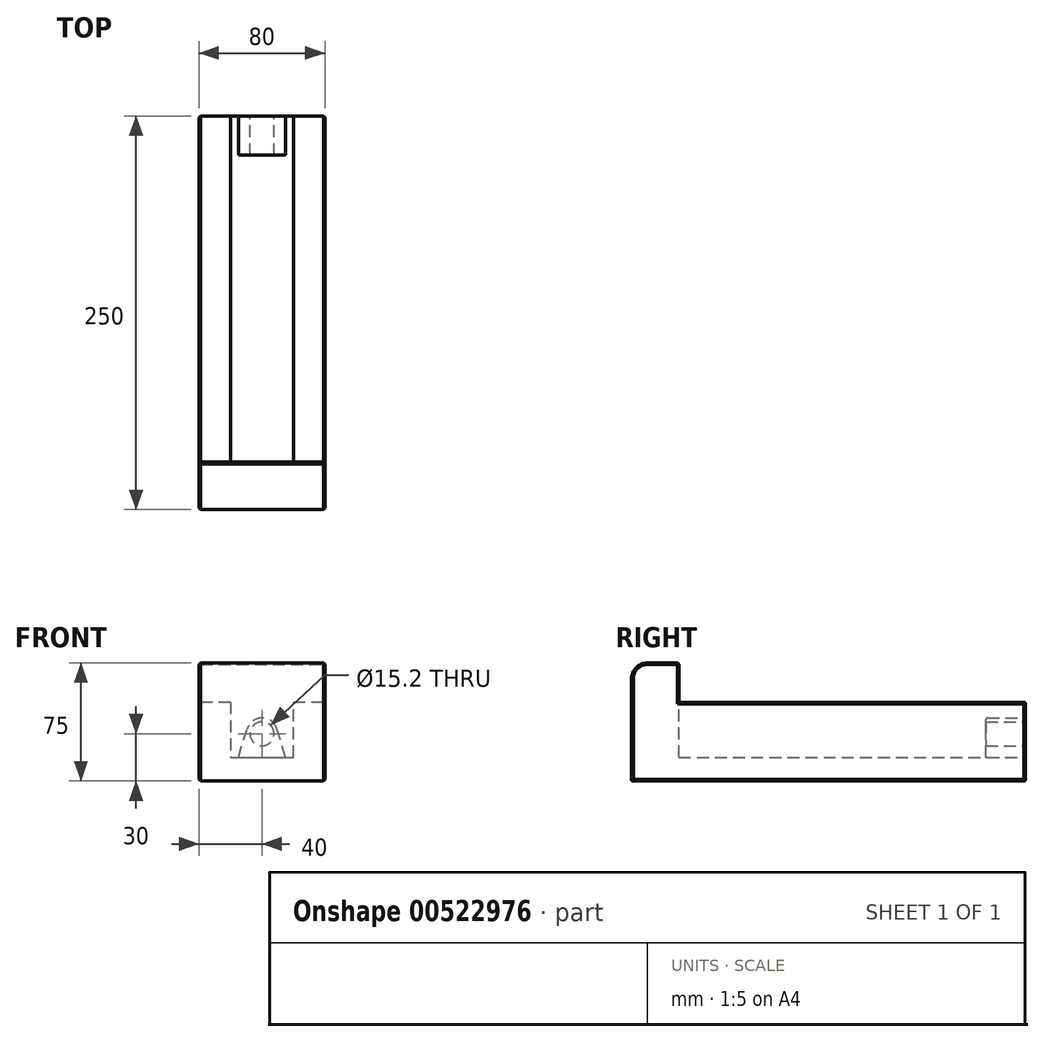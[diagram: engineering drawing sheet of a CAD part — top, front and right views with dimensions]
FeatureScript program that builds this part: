
annotation { "Feature Type Name" : "Feature", "Feature Type Description" : "" }
export const myFeature = defineFeature(function(context is Context, id is Id, definition is map)
    precondition{}
    {
        {
            var Q0;
            Q0=qCreatedBy(makeId("Right.planeOp"),FACE);
            var sketch = newSketch(context, id + "F0", { "sketchPlane" : qUnion([Q0])});
            skLineSegment(sketch, "E0", {"start": v(0, 0) * mm, "end": v(103.84, 0) * mm});
            skLineSegment(sketch, "E1", {"start": v(103.84, 0) * mm, "end": v(103.84, 50) * mm});
            skLineSegment(sketch, "E2", {"start": v(103.84, 50) * mm, "end": v(-116.16, 50) * mm});
            skLineSegment(sketch, "E3", {"start": v(-116.16, 50) * mm, "end": v(-116.16, 75) * mm});
            skLineSegment(sketch, "E4", {"start": v(-116.16, 75) * mm, "end": v(-136.16, 75) * mm});
            skLineSegment(sketch, "E5", {"start": v(-146.16, 65) * mm, "end": v(-146.16, 0) * mm});
            skLineSegment(sketch, "E6", {"start": v(-146.16, 0) * mm, "end": v(45.93, 0) * mm});
            skLineSegment(sketch, "E7", {"start": v(-146.16, 0) * mm, "end": v(103.84, 0) * mm});
            skPoint(sketch, "E8.visualSharp", {"position": v(-146.16, 75) * mm});
            skArc(sketch, "E8.filletArc", {"start": v(-136.16, 75) * mm, "mid": v(-143.23, 72.07) * mm, "end": v(-146.16, 65) * mm});
            skSolve(sketch);
        }
        {
            var Q0;
            Q0 = qSketchRegion(id + "F0", true);
            extrude(context, id + "F1", {"entities" : qUnion([Q0]), "endBound" : BoundingType.SYMMETRIC, "depth" : 80 * mm, "offsetDistance" : 25 * mm});
        }
        {
            var Q0;
            Q0=makeQuery(id+"F1.opExtrude","SWEPT_FACE",FACE,{"disambiguationData":[OSD([sQuery(id+"F0.wireOp",EDGE,"E1")])]});
            var sketch = newSketch(context, id + "F2", { "sketchPlane" : qUnion([Q0])});
            skLineSegment(sketch, "E9", {"start": v(20, 50) * mm, "end": v(20, 15) * mm});
            skLineSegment(sketch, "E10", {"start": v(20, 15) * mm, "end": v(-20, 15) * mm});
            skLineSegment(sketch, "E11", {"start": v(-20, 15) * mm, "end": v(-20, 50) * mm});
            skCircle(sketch, "E12", {"center": v(0, 30) * mm, "radius": 10 * mm});
            skPoint(sketch, "E12.centerSnap0", {"position": v(0, 15) * mm});
            skLineSegment(sketch, "E13", {"start": v(-15, 15) * mm, "end": v(-9.57, 32.9) * mm});
            skLineSegment(sketch, "E14", {"start": v(15, 15) * mm, "end": v(9.57, 32.9) * mm});
            skLineSegment(sketch, "E15", {"start": v(-20, 50) * mm, "end": v(20, 50) * mm});
            skCircle(sketch, "E16", {"center": v(0, 30) * mm, "radius": 7.6 * mm});
            skSolve(sketch);
        }
        {
            var Q0;
            {var subQ2=sQuery(id+"F2.wireOp",EDGE,"E9");Q0=makeQuery(id+"F2.imprint","IMPRINT",FACE,{"disambiguationData":[TD([[makeQuery(id+"F2.imprint","IMPRINT",EDGE,{"derivedFrom":subQ2}),-1.0]])]});}
            var Q1;
            {var subQ4=sQuery(id+"F2.wireOp",EDGE,"E11");Q1=makeQuery(id+"F2.imprint","IMPRINT",FACE,{"disambiguationData":[TD([[makeQuery(id+"F2.imprint","IMPRINT",EDGE,{"derivedFrom":subQ4}),-1.0]])]});}
            var Q2;
            {var subQ0=sQuery(id+"F2.wireOp",EDGE,"E12");var subQ1=makeQuery(id+"F2.imprint","INTERSECT",VERTEX,{"derivedFrom":[subQ0,sQuery(id+"F2.wireOp",EDGE,"E14")]});Q2=makeQuery(id+"F2.imprint","IMPRINT",FACE,{"disambiguationData":[TD([[makeQuery(id+"F2.imprint","IMPRINT",EDGE,{"disambiguationData":[TD([[subQ1,-1.0]])],"derivedFrom":subQ0}),1.0]])]});}
            var Q3;
            {var subQ0=sQuery(id+"F2.wireOp",EDGE,"E13");Q3=makeQuery(id+"F2.imprint","IMPRINT",FACE,{"disambiguationData":[TD([[makeQuery(id+"F2.imprint","IMPRINT",EDGE,{"derivedFrom":subQ0}),-1.0]])]});}
            var Q4;
            Q4=makeQuery(id+"F2.imprint","IMPRINT",FACE,{"disambiguationData":[TD([[makeQuery(id+"F2.imprint","IMPRINT",EDGE,{"derivedFrom":sQuery(id+"F2.wireOp",EDGE,"E16")}),1.0]])]});
            var Q5;
            Q5=makeQuery(id+"F1.opExtrude","SWEPT_FACE",FACE,{"disambiguationData":[OSD([sQuery(id+"F0.wireOp",EDGE,"E3")])]});
            extrude(context, id + "F3", {"entities" : qUnion([Q0, Q1, Q2, Q3, Q4]), "operationType" : NewBodyOperationType.REMOVE, "endBound" : BoundingType.UP_TO_SURFACE, "oppositeDirection" : true, "depth" : 197 * mm, "endBoundEntityFace" : qUnion([Q5]), "offsetDistance" : 25 * mm});
        }
        {
            var Q0;
            {var subQ0=sQuery(id+"F2.wireOp",EDGE,"E13");Q0=makeQuery(id+"F2.imprint","IMPRINT",FACE,{"disambiguationData":[TD([[makeQuery(id+"F2.imprint","IMPRINT",EDGE,{"derivedFrom":subQ0}),-1.0]])]});}
            var Q1;
            {var subQ0=sQuery(id+"F2.wireOp",EDGE,"E12");var subQ1=makeQuery(id+"F2.imprint","INTERSECT",VERTEX,{"derivedFrom":[subQ0,sQuery(id+"F2.wireOp",EDGE,"E14")]});Q1=makeQuery(id+"F2.imprint","IMPRINT",FACE,{"disambiguationData":[TD([[makeQuery(id+"F2.imprint","IMPRINT",EDGE,{"disambiguationData":[TD([[subQ1,-1.0]])],"derivedFrom":subQ0}),1.0]])]});}
            extrude(context, id + "F4", {"entities" : qUnion([Q0, Q1]), "operationType" : NewBodyOperationType.ADD, "oppositeDirection" : true, "depth" : 25 * mm, "offsetDistance" : 25 * mm});
        }
        {
            var Q0;
            Q0=makeQuery(id+"F1.opExtrude","CAP_FACE",FACE,{"disambiguationData":[OSD([sQuery(id+"F0.wireOp",EDGE,"E1"),sQuery(id+"F0.wireOp",EDGE,"E2"),sQuery(id+"F0.wireOp",EDGE,"E3"),sQuery(id+"F0.wireOp",EDGE,"E4"),sQuery(id+"F0.wireOp",EDGE,"E5"),sQuery(id+"F0.wireOp",EDGE,"E7")])],"isStart":true});
            var Q1;
            Q1=makeQuery(id+"F1.opExtrude","SWEPT_FACE",FACE,{"disambiguationData":[OSD([sQuery(id+"F0.wireOp",EDGE,"E4")])]});
            var Q2;
            Q2=makeQuery(id+"F1.opExtrude","CAP_FACE",FACE,{"disambiguationData":[OSD([sQuery(id+"F0.wireOp",EDGE,"E1"),sQuery(id+"F0.wireOp",EDGE,"E2"),sQuery(id+"F0.wireOp",EDGE,"E3"),sQuery(id+"F0.wireOp",EDGE,"E4"),sQuery(id+"F0.wireOp",EDGE,"E5"),sQuery(id+"F0.wireOp",EDGE,"E7")])],"isStart":false});
            chamfer(context, id + "F5", {"entities" : qUnion([Q0, Q1, Q2]), "width" : 1 * mm, "tangentPropagation" : true});
        }
        {
            var Q0;
            Q0=makeQuery(id+"F4.opExtrude","CAP_EDGE",EDGE,{"disambiguationData":[OSD([sQuery(id+"F2.wireOp",EDGE,"E14")])],"isStart":true});
            var Q1;
            Q1=makeQuery(id+"F4.opExtrude","SWEPT_EDGE",EDGE,{"disambiguationData":[OSD([sQuery(id+"F2.wireOp",EDGE,"E10"),sQuery(id+"F2.wireOp",EDGE,"E14")])]});
            var Q2;
            Q2=makeQuery(id+"F4.opExtrude","SWEPT_EDGE",EDGE,{"disambiguationData":[OSD([sQuery(id+"F2.wireOp",EDGE,"E10"),sQuery(id+"F2.wireOp",EDGE,"E13")])]});
            var Q3;
            Q3=makeQuery(id+"F4.opExtrude","CAP_EDGE",EDGE,{"disambiguationData":[OSD([sQuery(id+"F2.wireOp",EDGE,"E12")])],"isStart":false});
            fillet(context, id + "F6", {"entities" : qUnion([Q0, Q1, Q2, Q3]), "radius" : 1 * mm, "tangentPropagation" : true, "allowEdgeOverflow" : false});
        }
    });
